# Revit family: Konsole 45- 26 S
name_source: partatom
category: HLS-Bauteile
revit_build: Autodesk Revit 2017 (Build: 20190508_0315(x64)
units: mm (PartAtom-declared; Revit-internal decimal feet)

## family parameters
Basisbauteil = Fläche
Beim Laden mit Abzugskörper schneiden = Nein
Bemaßung runder Anschluss = Durchmesser verwenden
Gemeinsam genutzt = Ja
Raumberechnungspunkt = Nein
Teiletyp = Normal

## types (4) — shared parameters
Ausrichtung Platte = längs
Breite Platte = 50 mm  [stored 0.164042 ft]
Breite Profil = 45 mm  [stored 0.147638 ft]
Fabrikat = MEFA
Firma = MEFA Befestigungs- und Montagesysteme GmbH
Höhe Profil = 26 mm  [stored 0.0853018 ft]
Kurztext1 = Konsole C-Profil 45/26 S
Langloch Platte = 11x15 mm
Lochabstand = 66 mm
Länge Platte = 93 mm
Material = Stahl
Materialname C-Profil = S235
Materialname Platte = S355
Profil = C-Profil
Stärke Platte = 3 mm  [stored 0.00984252 ft]
Stärke Profil = 2 mm  [stored 0.00656168 ft]
Vorgabe-Ansicht = 1219 mm

## per-type parameters (varying)
| type | Artikelnummer | EAN | Gewicht | Gewicht pro Bauteil | Kurztext2 | Länge Konsole | Schienenlänge | max. zul. Last F1 | max. zul. Last F2 | max. zul. Last q0 |
| Konsole 45- 26 S L= 210 gvz | 18035021001 | 4250928456731 | 0.42 kg | 0.42 kg | L= 210 mm Platte längs gvz | 210 mm  [stored 0.688976 ft] | Montageschiene 45- 26-1,5 für Konsole : C-Profil 45- 26-1,5 L=  210 | 0.27 kip | 0.13 kip | 0.384 kip/ft |
| Konsole 45- 26 S L= 315 gvz | 18035031501 | 4250928456489 | 0.56 kg | 0.56 kg | L= 315 mm Platte längs gvz | 315 mm  [stored 1.03346 ft] | Montageschiene 45- 26-1,5 für Konsole : C-Profil 45- 26-1,5 L=  315 | 0.18 kip | 0.09 kip | 0.171 kip/ft |
| Konsole 45- 26 S L= 420 gvz | 18035042001 | 4250928456472 | 0.70 kg | 0.70 kg | L= 420 mm Platte längs gvz | 420 mm  [stored 1.37795 ft] | Montageschiene 45- 26-1,5 für Konsole : C-Profil 45- 26-1,5 L=  420 | 0.13 kip | 0.07 kip | 0.096 kip/ft |
| Konsole 45- 26 S L= 525 gvz | 18035052501 | 4250928456465 | 0.84 kg | 0.84 kg | L= 525 mm Platte längs gvz | 525 mm | Montageschiene 45- 26-1,5 für Konsole : C-Profil 45- 26-1,5 L=  525 | 0.11 kip | 0.05 kip | 0.062 kip/ft |

note: [stored X ft] marks values corroborated as IEEE doubles in the binary element streams (Revit-internal decimal feet)
